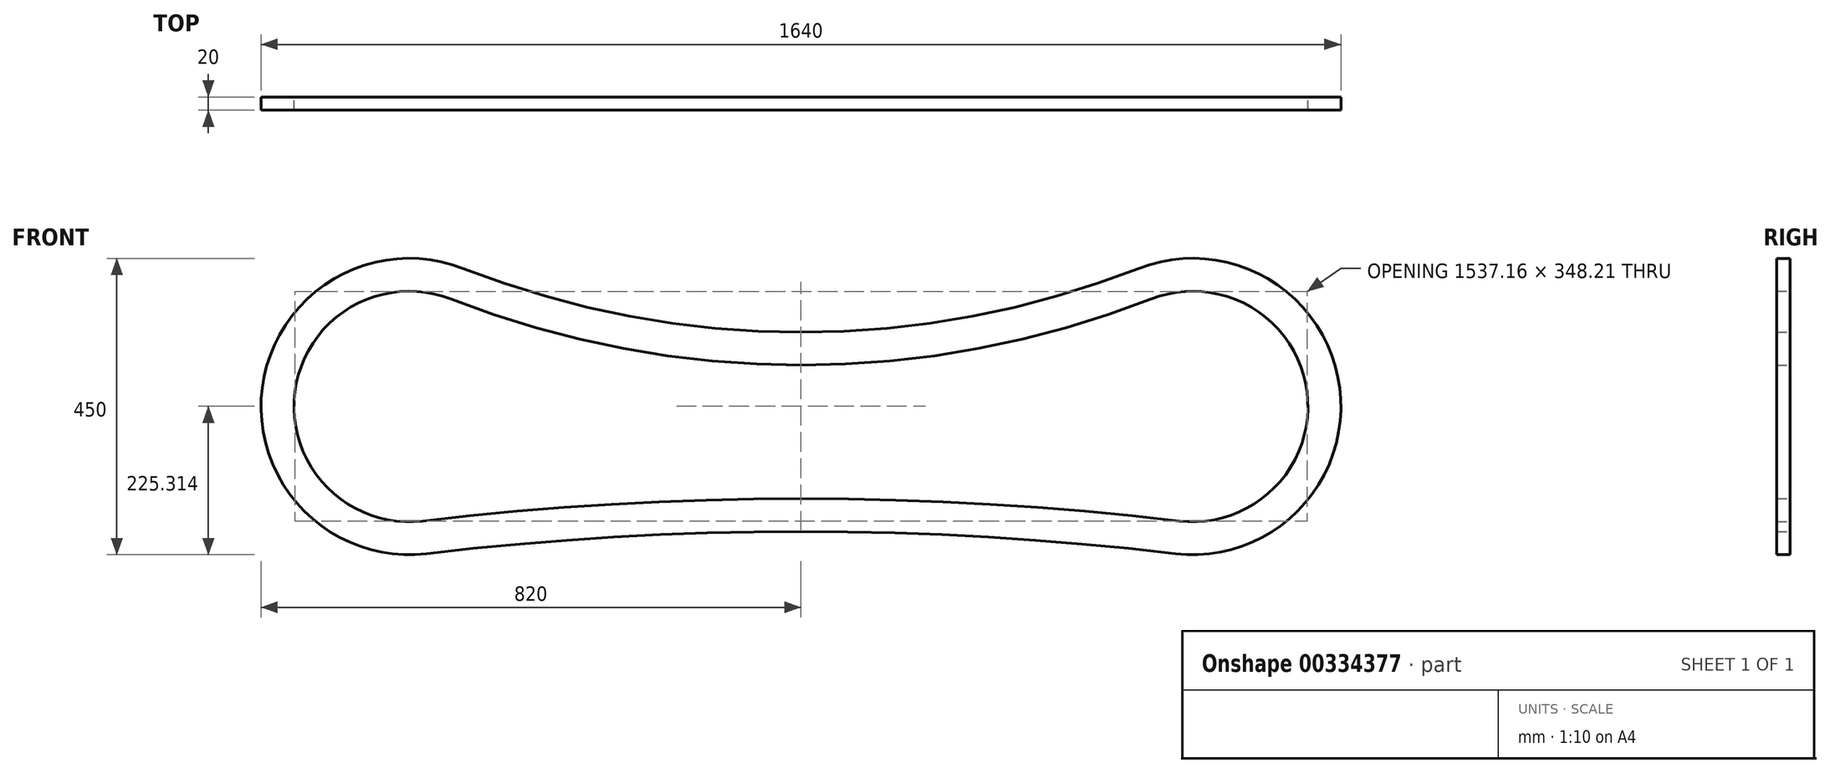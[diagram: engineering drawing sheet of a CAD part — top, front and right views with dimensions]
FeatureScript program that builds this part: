
annotation { "Feature Type Name" : "Feature", "Feature Type Description" : "" }
export const myFeature = defineFeature(function(context is Context, id is Id, definition is map)
    precondition{}
    {
        {
            var Q0;
            Q0=qCreatedBy(makeId("Front.planeOp"),FACE);
            var sketch = newSketch(context, id + "F0", { "sketchPlane" : qUnion([Q0])});
            skArc(sketch, "E0", {"start": v(-513.08, 209.56) * mm, "mid": v(-818.17, 28.63) * mm, "end": v(-568.62, -223.45) * mm});
            skArc(sketch, "E1", {"start": v(568.62, -223.45) * mm, "mid": v(818.17, 28.63) * mm, "end": v(513.08, 209.56) * mm});
            skArc(sketch, "E2", {"start": v(568.62, -223.45) * mm, "mid": v(0, -190) * mm, "end": v(-568.62, -223.45) * mm});
            skPoint(sketch, "E2.centerSnap0", {"position": v(0, 0) * mm});
            skArc(sketch, "E3", {"start": v(-513.08, 209.56) * mm, "mid": v(0, 112.83) * mm, "end": v(513.08, 209.56) * mm});
            skArc(sketch, "E4.0", {"start": v(-531.28, 162.99) * mm, "mid": v(-768.58, 22.26) * mm, "end": v(-574.48, -173.8) * mm});
            skArc(sketch, "E4.1", {"start": v(-531.28, 162.99) * mm, "mid": v(0, 62.83) * mm, "end": v(531.28, 162.99) * mm});
            skArc(sketch, "E4.2", {"start": v(574.48, -173.8) * mm, "mid": v(768.58, 22.26) * mm, "end": v(531.28, 162.99) * mm});
            skArc(sketch, "E4.3", {"start": v(574.48, -173.8) * mm, "mid": v(0, -140) * mm, "end": v(-574.48, -173.8) * mm});
            skSolve(sketch);
        }
        {
            var Q0;
            Q0=makeQuery(id+"F0.imprint","IMPRINT",FACE,{"disambiguationData":[TD([[makeQuery(id+"F0.imprint","IMPRINT",EDGE,{"derivedFrom":sQuery(id+"F0.wireOp",EDGE,"E0")}),1.0]])]});
            extrude(context, id + "F1", {"entities" : qUnion([Q0]), "depth" : 20 * mm});
        }
    });
